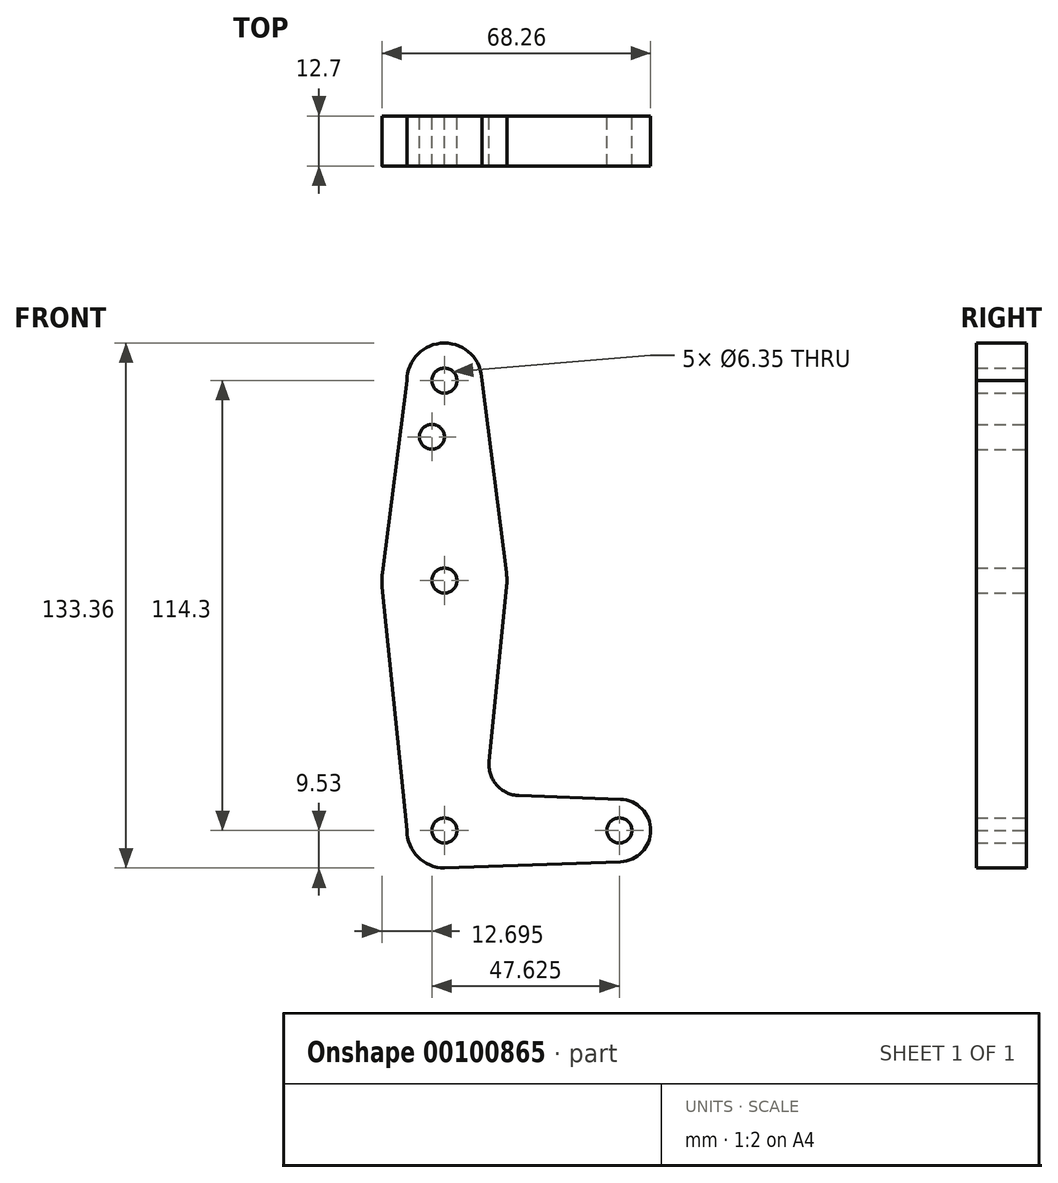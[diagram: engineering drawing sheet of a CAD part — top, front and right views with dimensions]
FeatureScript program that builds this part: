
annotation { "Feature Type Name" : "Feature", "Feature Type Description" : "" }
export const myFeature = defineFeature(function(context is Context, id is Id, definition is map)
    precondition{}
    {
        {
            var Q0;
            Q0=qCreatedBy(makeId("Front.planeOp"),FACE);
            var sketch = newSketch(context, id + "F0", { "sketchPlane" : qUnion([Q0])});
            skLineSegment(sketch, "E0", {"start": v(0, 0) * mm, "end": v(0, 114.3) * mm});
            skLineSegment(sketch, "E1", {"start": v(0, 0) * mm, "end": v(44.45, 0) * mm});
            skCircle(sketch, "E2", {"center": v(0, 114.3) * mm, "radius": 9.53 * mm});
            skCircle(sketch, "E3", {"center": v(0, 0) * mm, "radius": 9.53 * mm});
            skCircle(sketch, "E4", {"center": v(44.45, 0) * mm, "radius": 7.94 * mm});
            skCircle(sketch, "E5", {"center": v(0, 63.5) * mm, "radius": 15.88 * mm});
            skLineSegment(sketch, "E6", {"start": v(-9.53, 114.3) * mm, "end": v(-15.75, 65.5) * mm});
            skLineSegment(sketch, "E7", {"start": v(15.75, 65.5) * mm, "end": v(9.52, 114.3) * mm});
            skLineSegment(sketch, "E8", {"start": v(-15.8, 61.9) * mm, "end": v(-9.53, 0) * mm});
            skLineSegment(sketch, "E9", {"start": v(15.8, 61.91) * mm, "end": v(11.34, 17.6) * mm});
            skLineSegment(sketch, "E10", {"start": v(44.73, 7.93) * mm, "end": v(18.97, 8.85) * mm});
            skLineSegment(sketch, "E11", {"start": v(0, -9.53) * mm, "end": v(44.73, -7.93) * mm});
            skCircle(sketch, "E12", {"center": v(0, 114.3) * mm, "radius": 3.18 * mm});
            skCircle(sketch, "E13", {"center": v(0, 63.5) * mm, "radius": 3.18 * mm});
            skCircle(sketch, "E14", {"center": v(0, 0) * mm, "radius": 3.18 * mm});
            skCircle(sketch, "E15", {"center": v(44.45, 0) * mm, "radius": 3.18 * mm});
            skCircle(sketch, "E16", {"center": v(-3.17, 100.03) * mm, "radius": 3.18 * mm});
            skArc(sketch, "E17.filletArc", {"start": v(11.34, 17.6) * mm, "mid": v(13.26, 11.57) * mm, "end": v(18.97, 8.85) * mm});
            skSolve(sketch);
        }
        {
            var Q0;
            {var subQ0=sQuery(id+"F0.wireOp",EDGE,"E14");var subQ1=sQuery(id+"F0.wireOp",EDGE,"E0");var subQ2=makeQuery(id+"F0.imprint","INTERSECT",VERTEX,{"derivedFrom":[subQ1,subQ0]});Q0=makeQuery(id+"F0.imprint","IMPRINT",FACE,{"disambiguationData":[TD([[makeQuery(id+"F0.imprint","IMPRINT",EDGE,{"disambiguationData":[TD([[subQ2,-1.0]])],"derivedFrom":subQ1}),-1.0]])]});}
            var Q1;
            {var subQ2=sQuery(id+"F0.wireOp",EDGE,"E0");var subQ4=sQuery(id+"F0.wireOp",EDGE,"E14");var subQ11=makeQuery(id+"F0.imprint","INTERSECT",VERTEX,{"derivedFrom":[subQ2,subQ4]});Q1=makeQuery(id+"F0.imprint","IMPRINT",FACE,{"disambiguationData":[TD([[makeQuery(id+"F0.imprint","IMPRINT",EDGE,{"disambiguationData":[TD([[subQ11,-1.0]])],"derivedFrom":subQ2}),1.0]])]});}
            var Q2;
            {var subQ5=sQuery(id+"F0.wireOp",EDGE,"E8");Q2=makeQuery(id+"F0.imprint","IMPRINT",FACE,{"disambiguationData":[TD([[makeQuery(id+"F0.imprint","IMPRINT",EDGE,{"derivedFrom":subQ5}),1.0]])]});}
            var Q3;
            {var subQ10=sQuery(id+"F0.wireOp",EDGE,"E9");Q3=makeQuery(id+"F0.imprint","IMPRINT",FACE,{"disambiguationData":[TD([[makeQuery(id+"F0.imprint","IMPRINT",EDGE,{"derivedFrom":subQ10}),-1.0]])]});}
            var Q4;
            {var subQ0=sQuery(id+"F0.wireOp",EDGE,"E4");var subQ1=sQuery(id+"F0.wireOp",EDGE,"E1");var subQ2=makeQuery(id+"F0.imprint","INTERSECT",VERTEX,{"derivedFrom":[subQ1,subQ0]});Q4=makeQuery(id+"F0.imprint","IMPRINT",FACE,{"disambiguationData":[TD([[makeQuery(id+"F0.imprint","IMPRINT",EDGE,{"disambiguationData":[TD([[subQ2,1.0]])],"derivedFrom":subQ1}),-1.0]])]});}
            var Q5;
            Q5=makeQuery(id+"F0.imprint","IMPRINT",FACE,{"disambiguationData":[TD([[makeQuery(id+"F0.imprint","IMPRINT",EDGE,{"derivedFrom":sQuery(id+"F0.wireOp",EDGE,"E15")}),-1.0]])]});
            var Q6;
            {var subQ0=sQuery(id+"F0.wireOp",EDGE,"E5");var subQ2=sQuery(id+"F0.wireOp",EDGE,"E0");var subQ3=makeQuery(id+"F0.imprint","INTERSECT",VERTEX,{"disambiguationData":[OD(0.0)],"derivedFrom":[subQ2,subQ0]});Q6=makeQuery(id+"F0.imprint","IMPRINT",FACE,{"disambiguationData":[TD([[makeQuery(id+"F0.imprint","IMPRINT",EDGE,{"disambiguationData":[TD([[subQ3,-1.0]])],"derivedFrom":subQ2}),-1.0]])]});}
            var Q7;
            {var subQ0=sQuery(id+"F0.wireOp",EDGE,"E5");var subQ4=sQuery(id+"F0.wireOp",EDGE,"E0");var subQ8=makeQuery(id+"F0.imprint","INTERSECT",VERTEX,{"disambiguationData":[OD(0.0)],"derivedFrom":[subQ4,subQ0]});Q7=makeQuery(id+"F0.imprint","IMPRINT",FACE,{"disambiguationData":[TD([[makeQuery(id+"F0.imprint","IMPRINT",EDGE,{"disambiguationData":[TD([[subQ8,-1.0]])],"derivedFrom":subQ4}),1.0]])]});}
            var Q8;
            {var subQ0=sQuery(id+"F0.wireOp",EDGE,"E7");Q8=makeQuery(id+"F0.imprint","IMPRINT",FACE,{"disambiguationData":[TD([[makeQuery(id+"F0.imprint","IMPRINT",EDGE,{"derivedFrom":subQ0}),1.0]])]});}
            var Q9;
            {var subQ0=sQuery(id+"F0.wireOp",EDGE,"E6");Q9=makeQuery(id+"F0.imprint","IMPRINT",FACE,{"disambiguationData":[TD([[makeQuery(id+"F0.imprint","IMPRINT",EDGE,{"derivedFrom":subQ0}),1.0]])]});}
            var Q10;
            Q10=makeQuery(id+"F0.imprint","IMPRINT",FACE,{"disambiguationData":[TD([[makeQuery(id+"F0.imprint","IMPRINT",EDGE,{"derivedFrom":sQuery(id+"F0.wireOp",EDGE,"E12")}),-1.0]])]});
            var Q11;
            Q11 = qSketchRegion(id + "F2", true);
            extrude(context, id + "F1", {"entities" : qUnion([Q0, Q1, Q2, Q3, Q4, Q5, Q6, Q7, Q8, Q9, Q10, Q11]), "depth" : 12.7 * mm});
        }
    });
